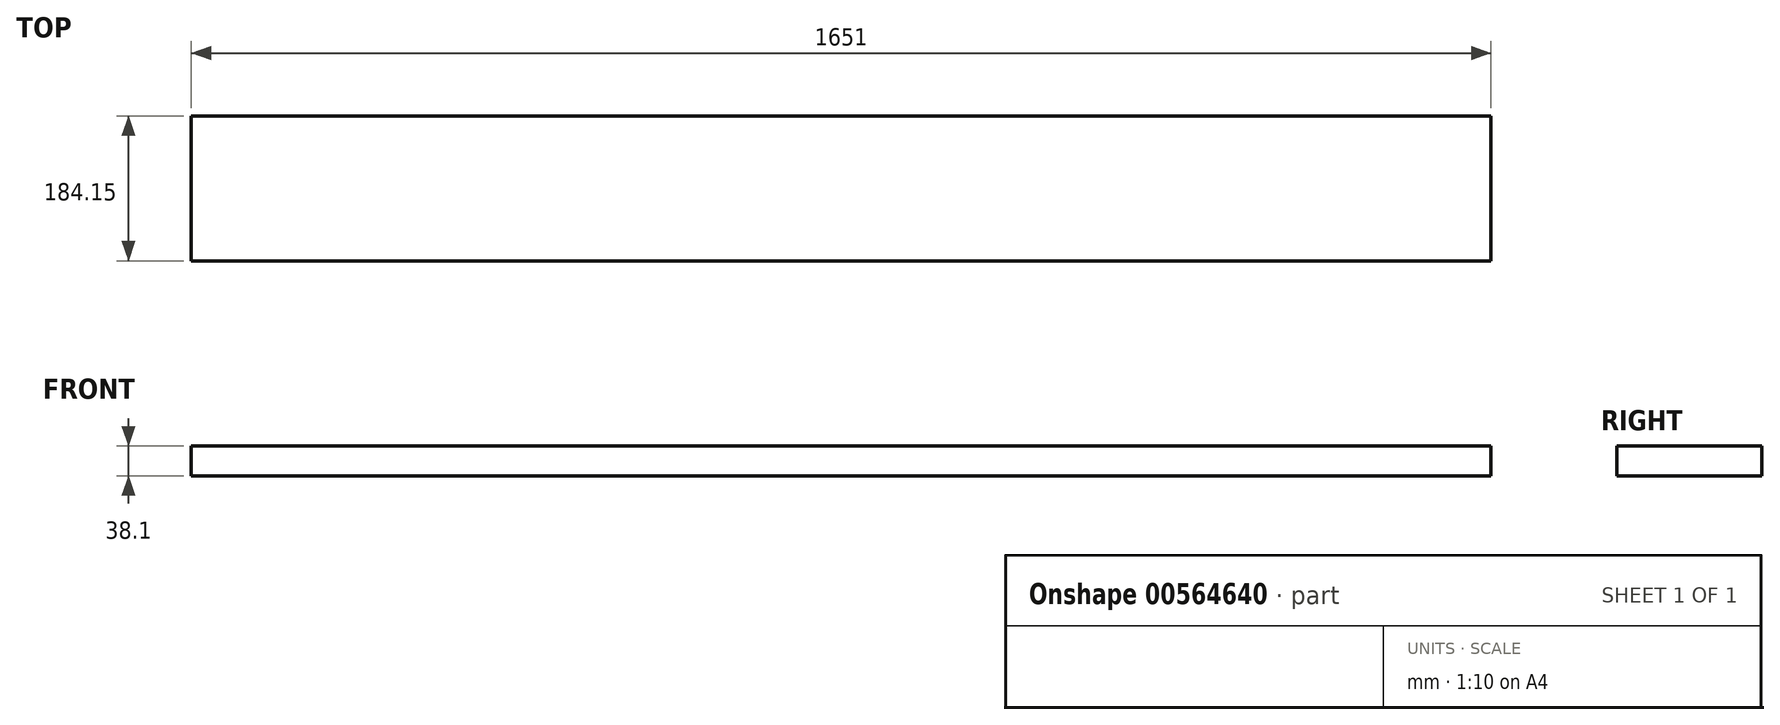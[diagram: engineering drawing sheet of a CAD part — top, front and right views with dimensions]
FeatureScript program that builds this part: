
annotation { "Feature Type Name" : "Feature", "Feature Type Description" : "" }
export const myFeature = defineFeature(function(context is Context, id is Id, definition is map)
    precondition{}
    {
        {
            var Q0;
            Q0=qCreatedBy(makeId("Top.planeOp"),FACE);
            var sketch = newSketch(context, id + "F0", { "sketchPlane" : qUnion([Q0])});
            skLineSegment(sketch, "E0.bottom", {"start": v(0, 0) * mm, "end": v(1651, 0) * mm});
            skLineSegment(sketch, "E0.top", {"start": v(0, 184.15) * mm, "end": v(1651, 184.15) * mm});
            skLineSegment(sketch, "E0.left", {"start": v(0, 0) * mm, "end": v(0, 184.15) * mm});
            skLineSegment(sketch, "E0.right", {"start": v(1651, 0) * mm, "end": v(1651, 184.15) * mm});
            skSolve(sketch);
        }
        {
            var Q0;
            Q0=makeQuery(id+"F0.imprint","IMPRINT",FACE,{"disambiguationData":[TD([[makeQuery(id+"F0.imprint","IMPRINT",EDGE,{"derivedFrom":sQuery(id+"F0.wireOp",EDGE,"E0.bottom")}),1.0]])]});
            extrude(context, id + "F1", {"entities" : qUnion([Q0]), "depth" : 38.1 * mm, "offsetDistance" : 25.4 * mm});
        }
    });
